# Revit family: 23799-Deca_Cuba Retangular de Embutir 60cm com Deck Duplo_Slim_L33060
name_source: partatom
category: Plumbing Fixtures
units: mm (PartAtom-declared; Revit-internal decimal feet)

## family parameters
Cut with Voids When Loaded = Yes
Host = Face
Part Type = Normal
Room Calculation Point = No
Round Connector Dimension = Use Radius
Shared = No

## types (4) — shared parameters
Acompanha o Produto = -
Aprovado por = quattroD
Atendimento ao Cliente = 0800-0117073
Composição Anel Vedação = -
Composição Assento = -
Composição Básica = Argila, feldspato, caulim, vidrados e corantes inorgânicos.
Composição Componente = Liga de elastômeros e plásticos de engenharia.
Consumo = -
Cor Secundária = -
Cores Componente = -
Criado por = quattroD
Código Pai = L.33060.MDE.17
Informações Complementares = -
Linha = Slim
Manufacturer = Deca
Peso Líquido (Kg) = 13.9
Pressão máx. funcionamento = 40 MCA
Pressão mín. Aquec. Acúmulo = -
Pressão mín. Aquec. Passagem = -
Pressão mín. funcionamento = 3 MCA
Saída de Esgoto = Válvula Curta
Segmento = Banheiro Luxo
Tipo de dispositivo economizador = -
Tipo de mecanismo utilizado = -
Tipo de rosca de entrada = -
Tipo de rosca de saída = -
URL = www.deca.com.br
Vazão na Pressão máx. (L/min) = -
Vazão na Pressão mín. (L/min) = -
zero-valued in all types: Default Elevation, Diâmetro Ponto de Esgoto, Raio Ponto de Esgoto

## per-type parameters (varying)
| type | Cor Interna | Cor Principal | Description | Material | Model |
| L.33060.MDE.17_Branco | branco | branco | Cuba Slim Retangular de Embutir 60cm com Deck Duplo Branco | Deca_Branco | L.33060.MDE.17 |
| L.33060.MDE.94_Ébano Fosco | ébano fosco | ébano fosco | Cuba Slim Retangular de Embutir 60cm com Deck Duplo Ébano Fosco | Deca_Ébano Fosco | L.33060.MDE.94 |
| L.33060.MDE.85_Soft Antracite | soft antracite | soft antracite | Cuba Slim Retangular de Embutir 60cm com Deck Duplo Soft Antracite | Deca_Soft Antracite | L.33060.MDE.85 |
| L.33060.MDE.26_Barbante | barbante | barbante | Cuba Slim Retangular de Embutir 60cm com Deck Duplo Barbante | Deca_Barbante | L.33060.MDE.26 |

## geometry (parser evidence)
native form markers: Sweep x3
no freeform markers — native parametric forms only
